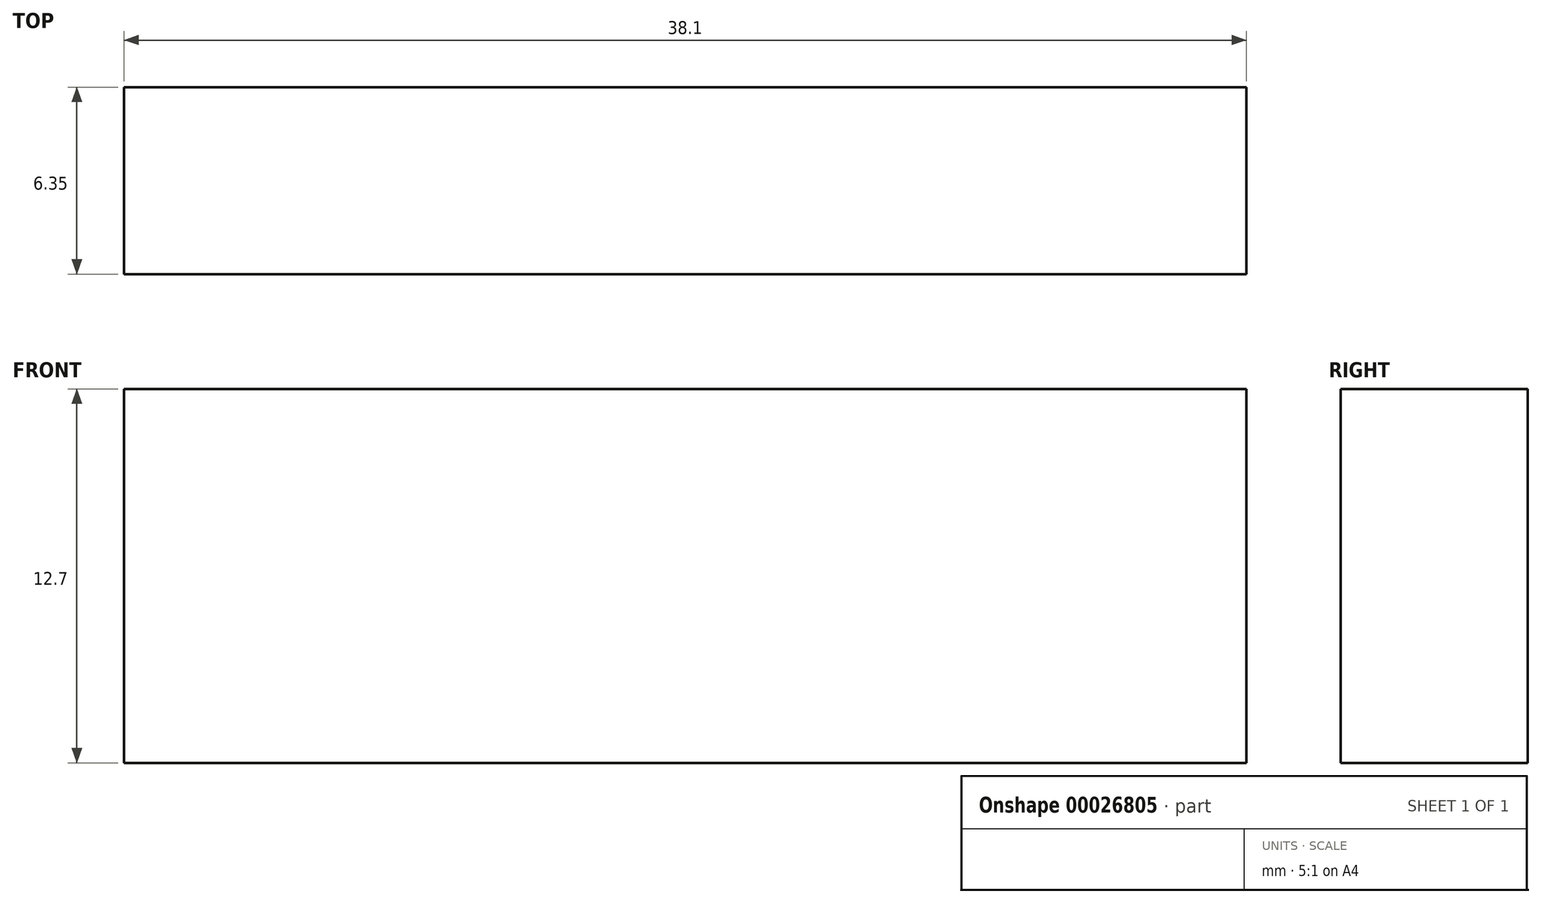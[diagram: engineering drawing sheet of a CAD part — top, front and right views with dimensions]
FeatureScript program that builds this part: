
annotation { "Feature Type Name" : "Feature", "Feature Type Description" : "" }
export const myFeature = defineFeature(function(context is Context, id is Id, definition is map)
    precondition{}
    {
        {
            var Q0;
            Q0=qCreatedBy(makeId("Front.planeOp"),FACE);
            var sketch = newSketch(context, id + "F0", { "sketchPlane" : qUnion([Q0])});
            skLineSegment(sketch, "E0.bottom", {"start": v(-38.06, 53.25) * mm, "end": v(0.04, 53.25) * mm});
            skLineSegment(sketch, "E0.top", {"start": v(-38.06, 40.55) * mm, "end": v(0.04, 40.55) * mm});
            skLineSegment(sketch, "E0.left", {"start": v(-38.06, 53.25) * mm, "end": v(-38.06, 40.55) * mm});
            skLineSegment(sketch, "E0.right", {"start": v(0.04, 53.25) * mm, "end": v(0.04, 40.55) * mm});
            skSolve(sketch);
        }
        {
            var Q0;
            Q0=makeQuery(id+"F0.imprint","IMPRINT",FACE,{"disambiguationData":[TD([[makeQuery(id+"F0.imprint","IMPRINT",EDGE,{"derivedFrom":sQuery(id+"F0.wireOp",EDGE,"E0.bottom")}),-1.0]])]});
            extrude(context, id + "F1", {"entities" : qUnion([Q0]), "depth" : 6.35 * mm});
        }
    });
